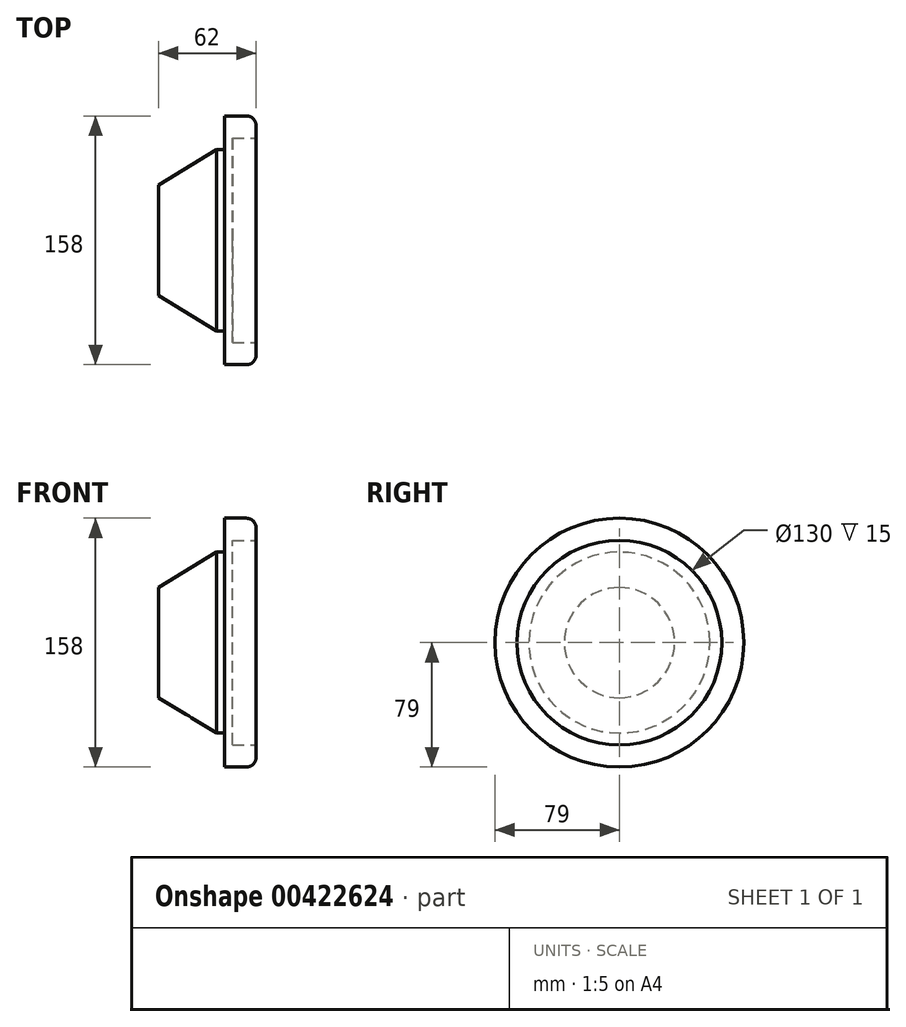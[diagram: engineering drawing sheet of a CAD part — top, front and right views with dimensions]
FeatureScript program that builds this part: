
annotation { "Feature Type Name" : "Feature", "Feature Type Description" : "" }
export const myFeature = defineFeature(function(context is Context, id is Id, definition is map)
    precondition{}
    {
        {
            var Q0;
            Q0=qCreatedBy(makeId("Right.planeOp"),FACE);
            var sketch = newSketch(context, id + "F0", { "sketchPlane" : qUnion([Q0])});
            skCircle(sketch, "E0", {"center": v(0, 0) * mm, "radius": 65 * mm});
            skSolve(sketch);
        }
        {
            var Q0;
            Q0=makeQuery(id+"F0.imprint","IMPRINT",FACE,{"disambiguationData":[TD([[makeQuery(id+"F0.imprint","IMPRINT",EDGE,{"derivedFrom":sQuery(id+"F0.wireOp",EDGE,"E0")}),1.0]])]});
            extrude(context, id + "F1", {"entities" : qUnion([Q0]), "depth" : 5 * mm});
        }
        {
            var Q0;
            Q0=qCreatedBy(makeId("Right.planeOp"),FACE);
            var sketch = newSketch(context, id + "F2", { "sketchPlane" : qUnion([Q0])});
            skCircle(sketch, "E1", {"center": v(0, 0) * mm, "radius": 57.5 * mm});
            skSolve(sketch);
        }
        {
            var Q0;
            Q0=makeQuery(id+"F2.imprint","IMPRINT",FACE,{"disambiguationData":[TD([[makeQuery(id+"F2.imprint","IMPRINT",EDGE,{"derivedFrom":sQuery(id+"F2.wireOp",EDGE,"E1")}),1.0]])]});
            extrude(context, id + "F3", {"entities" : qUnion([Q0]), "operationType" : NewBodyOperationType.ADD, "oppositeDirection" : true, "depth" : 5 * mm});
        }
        {
            var Q0;
            Q0=makeQuery(id+"F1.opExtrude","CAP_FACE",FACE,{"disambiguationData":[OSD([sQuery(id+"F0.wireOp",EDGE,"E0")])],"isStart":true});
            cPlane(context, id + "F4", {"entities" : qUnion([Q0]), "cplaneType" : CPlaneType.OFFSET, "offset" : 42 * mm, "width" : 150 * mm, "height" : 150 * mm});
        }
        {
            var Q0;
            Q0=qCreatedBy(id+"F4.planeOp",FACE);
            var sketch = newSketch(context, id + "F5", { "sketchPlane" : qUnion([Q0])});
            skCircle(sketch, "E2", {"center": v(0, 0) * mm, "radius": 35 * mm});
            skSolve(sketch);
        }
        {
            var Q1;
            Q1=makeQuery(id+"F3.opExtrude","CAP_FACE",FACE,{"disambiguationData":[OSD([sQuery(id+"F2.wireOp",EDGE,"E1")])],"isStart":false});
            var Q2;
            Q2=makeQuery(id+"F5.imprint","IMPRINT",FACE,{"disambiguationData":[TD([[makeQuery(id+"F5.imprint","IMPRINT",EDGE,{"derivedFrom":sQuery(id+"F5.wireOp",EDGE,"E2")}),1.0]])]});
            loft(context, id + "F6", {"operationType" : NewBodyOperationType.ADD, "sheetProfilesArray" : [{ "sheetProfileEntities" : qUnion([Q1]) }, { "sheetProfileEntities" : qUnion([Q2]) }]});
        }
        {
            var Q0;
            Q0=makeQuery(id+"F1.opExtrude","CAP_FACE",FACE,{"disambiguationData":[OSD([sQuery(id+"F0.wireOp",EDGE,"E0")])],"isStart":false});
            var sketch = newSketch(context, id + "F7", { "sketchPlane" : qUnion([Q0])});
            skCircle(sketch, "E3", {"center": v(0, 0) * mm, "radius": 79 * mm});
            skSolve(sketch);
        }
        {
            var Q0;
            Q0=makeQuery(id+"F7.imprint","IMPRINT",FACE,{"disambiguationData":[TD([[makeQuery(id+"F7.imprint","IMPRINT",EDGE,{"derivedFrom":sQuery(id+"F7.wireOp",EDGE,"E3")}),1.0]])]});
            extrude(context, id + "F8", {"entities" : qUnion([Q0]), "oppositeDirection" : true, "depth" : 5 * mm});
        }
        {
            var Q0;
            Q0=makeQuery(id+"F8.opExtrude","CAP_FACE",FACE,{"disambiguationData":[OSD([sQuery(id+"F0.wireOp",EDGE,"E0"),sQuery(id+"F7.wireOp",EDGE,"E3")])],"isStart":true});
            extrude(context, id + "F9", {"entities" : qUnion([Q0]), "operationType" : NewBodyOperationType.ADD, "depth" : 15 * mm});
        }
        {
            var Q0;
            Q0=makeQuery(id+"F9.opExtrude","CAP_EDGE",EDGE,{"disambiguationData":[OSD([sQuery(id+"F7.wireOp",EDGE,"E3")])],"isStart":false});
            fillet(context, id + "F10", {"entities" : qUnion([Q0]), "radius" : 6 * mm, "tangentPropagation" : true, "allowEdgeOverflow" : false});
        }
    });
